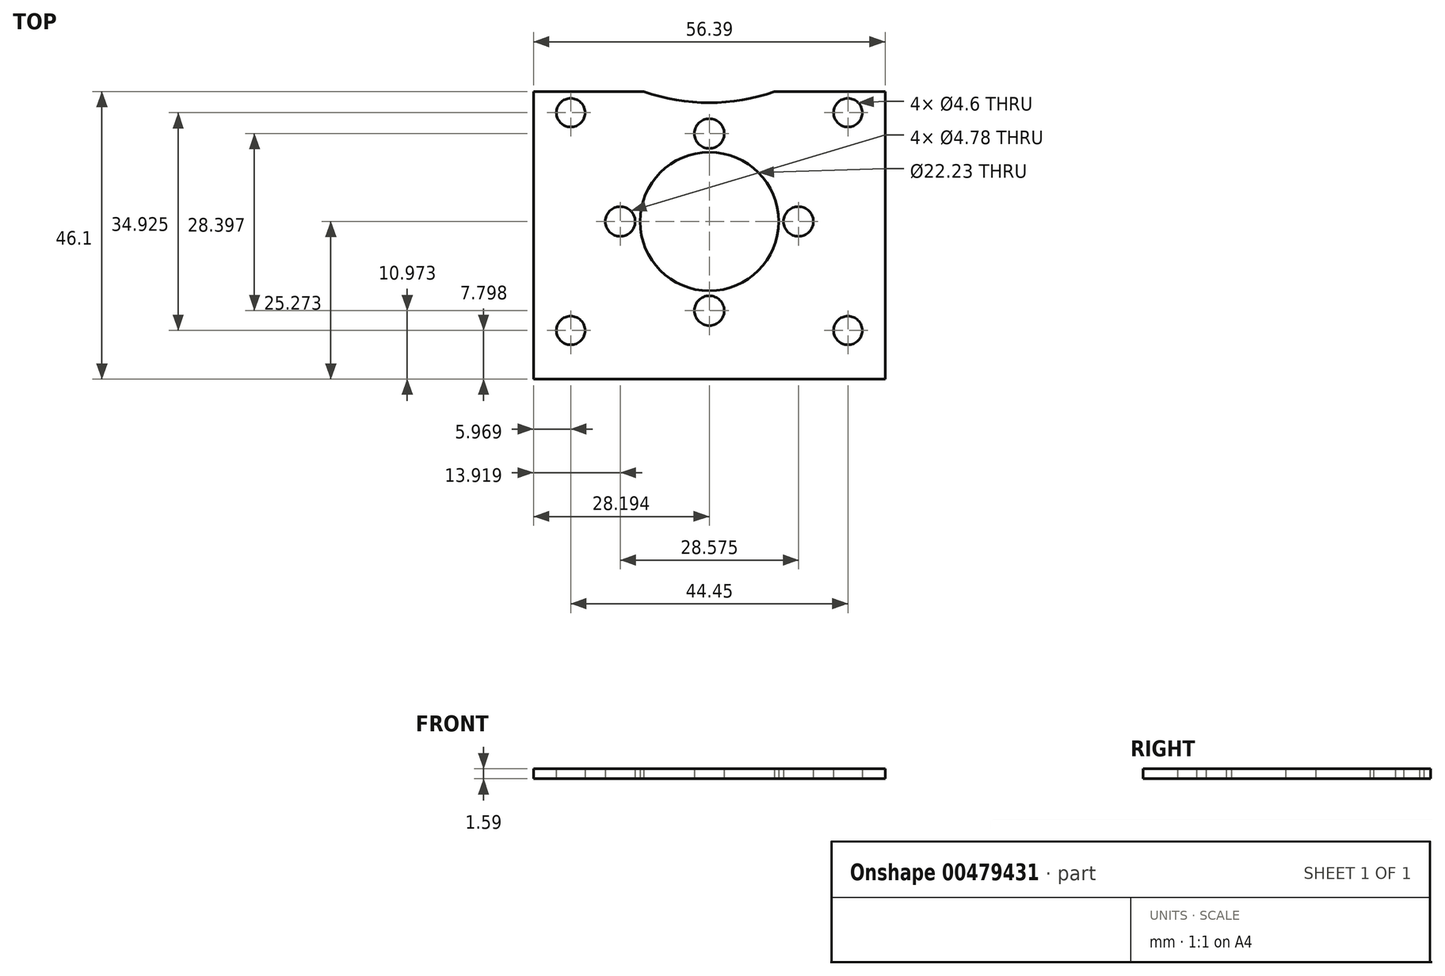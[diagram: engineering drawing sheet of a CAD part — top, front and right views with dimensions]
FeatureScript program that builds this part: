
annotation { "Feature Type Name" : "Feature", "Feature Type Description" : "" }
export const myFeature = defineFeature(function(context is Context, id is Id, definition is map)
    precondition{}
    {
        {
            var Q0;
            Q0=qCreatedBy(makeId("Top.planeOp"),FACE);
            var sketch = newSketch(context, id + "F0", { "sketchPlane" : qUnion([Q0]), "disableImprinting" : false});
            skLineSegment(sketch, "E0.bottom", {"start": v(0, 0) * mm, "end": v(56.39, 0) * mm});
            skLineSegment(sketch, "E0.top", {"start": v(0, 46.1) * mm, "end": v(56.39, 46.1) * mm});
            skLineSegment(sketch, "E0.left", {"start": v(0, 0) * mm, "end": v(0, 46.1) * mm});
            skLineSegment(sketch, "E0.right", {"start": v(56.39, 0) * mm, "end": v(56.39, 46.1) * mm});
            skCircle(sketch, "E1", {"center": v(28.2, 25.27) * mm, "radius": 11.11 * mm});
            skCircle(sketch, "E2", {"center": v(28.2, 10.97) * mm, "radius": 2.39 * mm});
            skCircle(sketch, "E3", {"center": v(50.42, 7.8) * mm, "radius": 2.3 * mm});
            skCircle(sketch, "E4", {"center": v(13.92, 25.27) * mm, "radius": 2.39 * mm});
            skCircle(sketch, "E5", {"center": v(5.97, 7.8) * mm, "radius": 2.3 * mm});
            skCircle(sketch, "E6", {"center": v(42.5, 25.27) * mm, "radius": 2.39 * mm});
            skCircle(sketch, "E7", {"center": v(-141.24, 13.59) * mm, "radius": 7.88 * mm});
            skCircle(sketch, "E8", {"center": v(28.2, 39.37) * mm, "radius": 2.39 * mm});
            skCircle(sketch, "E9", {"center": v(-136.96, -5.95) * mm, "radius": 8.13 * mm});
            skCircle(sketch, "E10", {"center": v(5.97, 42.72) * mm, "radius": 2.3 * mm});
            skCircle(sketch, "E11", {"center": v(50.42, 42.72) * mm, "radius": 2.3 * mm});
            skCircle(sketch, "E12", {"center": v(28.18, 76.07) * mm, "radius": 31.75 * mm});
            skPoint(sketch, "E13", {"position": v(17.7, 46.1) * mm});
            skPoint(sketch, "E14", {"position": v(38.66, 46.1) * mm});
            skSolve(sketch);
        }
        {
            var Q0;
            Q0=makeQuery(id+"F0.imprint","IMPRINT",FACE,{"disambiguationData":[TD([[makeQuery(id+"F0.imprint","IMPRINT",EDGE,{"derivedFrom":sQuery(id+"F0.wireOp",EDGE,"E0.bottom")}),1.0]])]});
            extrude(context, id + "F1", {"entities" : qUnion([Q0]), "depth" : 1.59 * mm, "offsetDistance" : 25.4 * mm});
        }
    });
